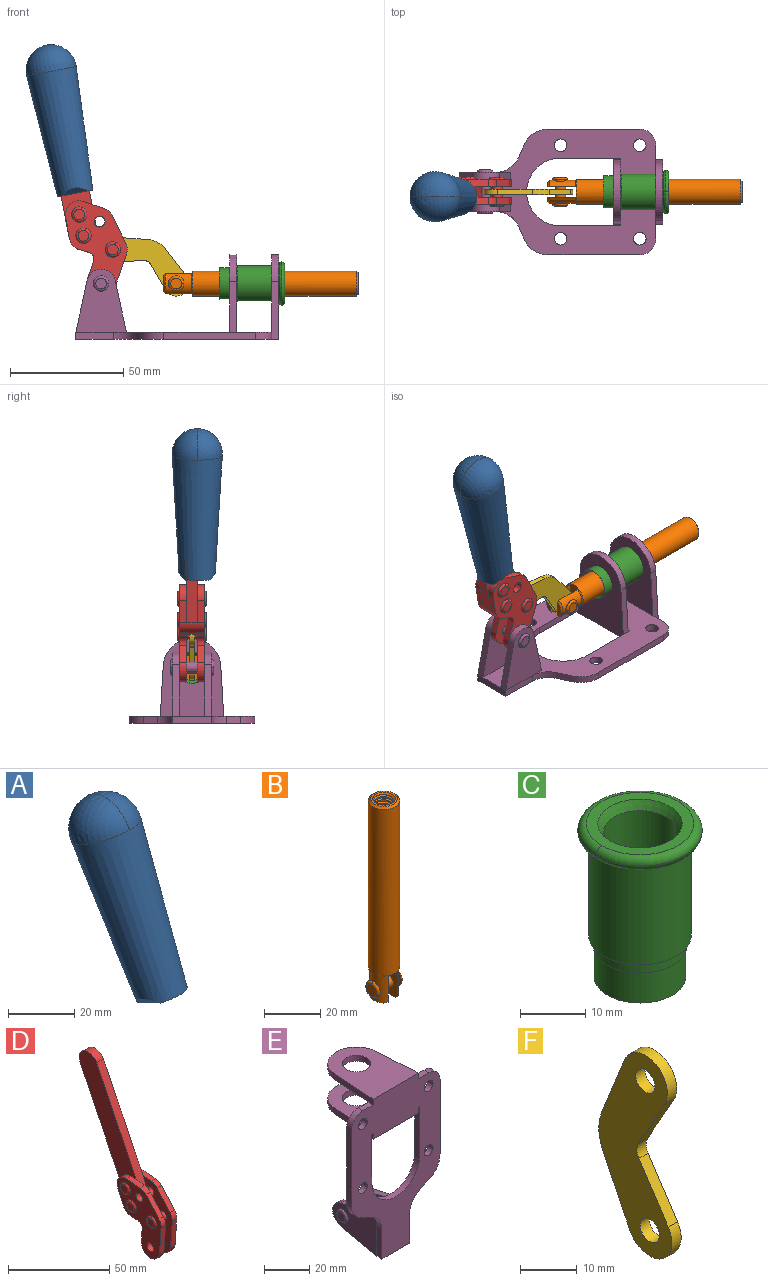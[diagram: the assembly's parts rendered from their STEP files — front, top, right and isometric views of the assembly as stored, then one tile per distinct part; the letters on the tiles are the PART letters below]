
ASSEMBLY  parts=6 mates=6
PART A: 11 faces, bbox 22.3x42.6x64.5 mm
  f0: sphere r=11.13mm, area 411.4mm2, adj f1,f8
  f1: cone r=11.11mm half-angle=3.3deg, axis (0,0.44,0.9), area 3251.8mm2, adj f0,f7,f8,f9,f10
  f2: cylinder r=6.16mm len=11.7mm, axis (1,0,0), area 89.5mm2, adj f3,f4,f5,f6
  f3: plane 60.23x36.75mm, normal (-1,0,0), area 763.6mm2, adj f2,f4,f6,f10
  f4: plane 51.37x25.05mm, normal (0,0.9,-0.44), area 264.2mm2, adj f2,f3,f5,f10
  f5: plane 60.23x36.75mm, normal (1,0,0), area 763.6mm2, adj f2,f4,f6,f10
  f6: plane 51.37x25.05mm, normal (0,-0.9,0.44), area 264.2mm2, adj f2,f3,f5,f10
  f7: plane 9.95x5.95mm, normal (0.71,-0.31,-0.64), area 25.8mm2, adj f1,f10
  f8: sphere r=11.13mm, area 411.4mm2, adj f0,f1
  f9: plane 9.95x5.95mm, normal (-0.71,-0.31,-0.64), area 25.8mm2, adj f1,f10
  f10: plane 14.27x11.38mm, normal (0,-0.44,-0.9), area 106.7mm2, adj f1,f3,f4,f5,f6,f7,f9
PART B: 48 faces, bbox 12.6x11.1x86.1 mm
  f0: torus R=2.41mm, axis (-1,0,0), area 15mm2, adj f30,f32,f34
  f1: torus R=2.41mm, axis (-1,0,0), area 15mm2, adj f29,f31,f33
  f2: cylinder r=5.54mm len=72.39mm, axis (0,0,1), area 2518.5mm2, adj f3,f4,f42,f43
  f3: cone r=5.54mm half-angle=45deg, axis (0,0,1), area 7.6mm2, adj f2,f5,f41
  f4: cone r=5.54mm half-angle=45deg, axis (0,0,-1), area 34.9mm2, adj f2,f39
  f5: cylinder r=5.08mm len=11.48mm, axis (0,0,1), area 108.3mm2, adj f3,f7,f8,f41
  f6: cylinder r=2.41mm len=4.83mm, axis (-1,0,0), area 71.2mm2, adj f40,f41
  f7: cylinder r=2.41mm len=4.83mm, axis (-1,0,0), area 7.6mm2, adj f5,f34
  f8: cone r=5.08mm half-angle=45deg, axis (0,0,1), area 10.6mm2, adj f5,f37,f41
  f9: cone r=3.98mm half-angle=45deg, axis (0,0,1), area 17.6mm2, adj f27,f39,f45,f46,f47
  f10: cylinder r=2.41mm len=4.83mm, axis (-1,0,0), area 7.6mm2, adj f33,f38
  f11: cylinder r=3.2mm len=6.4mm, axis (0,0,1), area 78.4mm2, adj f12,f28,f44,f45,f47
  f12: cylinder r=3.2mm len=6.4mm, axis (0,0,1), area 10.5mm2, adj f11,f13,f45,f47
  f13: cylinder r=3.2mm len=6.4mm, axis (0,0,1), area 10.5mm2, adj f12,f14,f45,f47
  f14: cylinder r=3.2mm len=6.4mm, axis (0,0,1), area 10.5mm2, adj f13,f15,f45,f47
  f15: cylinder r=3.2mm len=6.4mm, axis (0,0,1), area 10.5mm2, adj f14,f16,f45,f47
  f16: cylinder r=3.2mm len=6.4mm, axis (0,0,1), area 10.5mm2, adj f15,f17,f45,f47
  f17: cylinder r=3.2mm len=6.4mm, axis (0,0,1), area 10.5mm2, adj f16,f18,f45,f47
  f18: cylinder r=3.2mm len=6.4mm, axis (0,0,1), area 10.5mm2, adj f17,f19,f45,f47
  f19: cylinder r=3.2mm len=6.4mm, axis (0,0,1), area 10.5mm2, adj f18,f20,f45,f47
  f20: cylinder r=3.2mm len=6.4mm, axis (0,0,1), area 10.5mm2, adj f19,f21,f45,f47
  f21: cylinder r=3.2mm len=6.4mm, axis (0,0,1), area 10.5mm2, adj f20,f22,f45,f47
  f22: cylinder r=3.2mm len=6.4mm, axis (0,0,1), area 10.5mm2, adj f21,f23,f45,f47
  f23: cylinder r=3.2mm len=6.4mm, axis (0,0,1), area 10.5mm2, adj f22,f24,f45,f47
  f24: cylinder r=3.2mm len=6.4mm, axis (0,0,1), area 10.5mm2, adj f23,f25,f45,f47
  f25: cylinder r=3.2mm len=6.4mm, axis (0,0,1), area 10.5mm2, adj f24,f26,f45,f47
  f26: cylinder r=3.2mm len=6.4mm, axis (0,0,1), area 10.5mm2, adj f25,f27,f45,f47
  f27: cylinder r=3.2mm len=6.4mm, axis (0,0,1), area 7.4mm2, adj f9,f26,f45,f47
  f28: cone r=3.2mm half-angle=60deg, axis (0,0,1), area 37.2mm2, adj f11
  f29: plane 4.83x4.83mm, normal (-1,0,0), area 18.3mm2, adj f1,f31
  f30: plane 4.83x4.83mm, normal (1,0,0), area 18.3mm2, adj f0,f32
  f31: torus R=2.41mm, axis (-1,0,0), area 15mm2, adj f1,f29,f33
  f32: torus R=2.41mm, axis (-1,0,0), area 15mm2, adj f0,f30,f34
  f33: plane 6.83x6.83mm, normal (1,0,0), area 18.3mm2, adj f1,f10,f31
  f34: plane 6.83x6.83mm, normal (-1,0,0), area 18.3mm2, adj f0,f7,f32
  f35: cone r=5.08mm half-angle=45deg, axis (0,0,1), area 10.6mm2, adj f36,f38,f40
  f36: plane 7.25x1.97mm, normal (0,0,-1), area 10mm2, adj f35,f40
  f37: plane 7.25x1.97mm, normal (0,0,-1), area 10mm2, adj f8,f41
  f38: cylinder r=5.08mm len=11.48mm, axis (0,0,1), area 108.3mm2, adj f10,f35,f40,f42
  f39: plane 9.55x9.55mm, normal (0,0,1), area 22mm2, adj f4,f9
  f40: plane 12.76x10.09mm, normal (1,0,0), area 95.7mm2, adj f6,f35,f36,f38,f42,f43
  f41: plane 12.76x10.09mm, normal (-1,0,0), area 95.7mm2, adj f3,f5,f6,f8,f37,f43
  f42: cone r=5.54mm half-angle=45deg, axis (0,0,1), area 7.6mm2, adj f2,f38,f40
  f43: plane 11.07x4.7mm, normal (0,0,-1), area 50.4mm2, adj f2,f40,f41
  f44: plane 0.89x0.62mm, normal (-1,0,0), area 0.3mm2, adj f11,f45,f46,f47
  f45: bspline ~24.8x7.63mm, area 266.6mm2, adj f9,f11,f12,f13,f14,f15,f16,f17
  f46: bspline ~24.87x7.63mm, area 73.6mm2, adj f9,f44,f45,f47
  f47: bspline ~24.98x7.63mm, area 272.5mm2, adj f9,f11,f12,f13,f14,f15,f16,f17
PART C: 15 faces, bbox 20.6x20.6x28.7 mm
  f0: torus R=8.26mm, axis (0,0,1), area 56.8mm2, adj f1,f10,f12
  f1: torus R=8.26mm, axis (0,0,1), area 56.8mm2, adj f0,f6,f13
  f2: cylinder r=5.59mm len=25.91mm, axis (0,0,1), area 909.6mm2, adj f3,f4
  f3: cone r=6.86mm half-angle=45deg, axis (0,0,-1), area 70.2mm2, adj f2,f14
  f4: cone r=6.47mm half-angle=30deg, axis (0,0,1), area 66.7mm2, adj f2,f13
  f5: cylinder r=7.04mm len=14.07mm, axis (0,0,1), area 252.6mm2, adj f11,f14
  f6: torus R=8.26mm, axis (0,0,1), area 56.8mm2, adj f1,f12,f13
  f7: cylinder r=7.16mm len=14.33mm, axis (0,0,1), area 91.5mm2, adj f9,f11
  f8: cylinder r=7.86mm len=18.42mm, axis (0,0,1), area 909.6mm2, adj f9,f10
  f9: plane 15.72x15.72mm, normal (0,0,-1), area 33mm2, adj f7,f8
  f10: plane 16.51x16.51mm, normal (0,0,-1), area 19.9mm2, adj f0,f8,f12
  f11: plane 14.33x14.33mm, normal (0,0,-1), area 5.7mm2, adj f5,f7
  f12: torus R=8.26mm, axis (0,0,1), area 56.8mm2, adj f0,f6,f10
  f13: plane 16.51x16.51mm, normal (0,0,1), area 82.7mm2, adj f1,f4,f6
  f14: plane 14.07x14.07mm, normal (0,0,-1), area 7.8mm2, adj f3,f5
PART D: 59 faces, bbox 12.9x60.2x99.6 mm
  f0: torus R=2.39mm, axis (-1,0,0), area 14.9mm2, adj f20,f43,f51
  f1: torus R=2.39mm, axis (-1,0,0), area 14.9mm2, adj f19,f42,f51
  f2: torus R=2.39mm, axis (-1,0,0), area 14.9mm2, adj f18,f35,f51
  f3: torus R=2.39mm, axis (-1,0,0), area 14.9mm2, adj f14,f17,f23
  f4: torus R=2.39mm, axis (-1,0,0), area 14.9mm2, adj f13,f16,f23
  f5: torus R=2.39mm, axis (-1,0,0), area 14.9mm2, adj f12,f15,f23
  f6: cylinder r=2.39mm len=4.78mm, axis (1,0,0), area 46.5mm2, adj f48,f50,f51
  f7: cylinder r=2.39mm len=4.78mm, axis (1,0,0), area 46.5mm2, adj f50,f51
  f8: cylinder r=6.35mm len=12.68mm, axis (1,0,0), area 61.8mm2, adj f38,f39,f50,f51
  f9: cylinder r=2.39mm len=4.78mm, axis (-1,0,0), area 70.5mm2, adj f46,f50
  f10: cylinder r=2.39mm len=4.78mm, axis (-1,0,0), area 46.5mm2, adj f23,f45,f46
  f11: cylinder r=2.39mm len=4.78mm, axis (-1,0,0), area 46.5mm2, adj f23,f46
  f12: plane 4.78x4.78mm, normal (1,0,0), area 17.9mm2, adj f5,f15
  f13: plane 4.78x4.78mm, normal (1,0,0), area 17.9mm2, adj f4,f16
  f14: plane 4.78x4.78mm, normal (1,0,0), area 17.9mm2, adj f3,f17
  f15: torus R=2.39mm, axis (-1,0,0), area 14.9mm2, adj f5,f12,f23
  f16: torus R=2.39mm, axis (-1,0,0), area 14.9mm2, adj f4,f13,f23
  f17: torus R=2.39mm, axis (-1,0,0), area 14.9mm2, adj f3,f14,f23
  f18: plane 4.78x4.78mm, normal (-1,0,0), area 17.9mm2, adj f2,f35
  f19: plane 4.78x4.78mm, normal (-1,0,0), area 17.9mm2, adj f1,f42
  f20: plane 4.78x4.78mm, normal (-1,0,0), area 17.9mm2, adj f0,f43
  f21: plane 2.26x0.2mm, normal (1,0,0), area 0.2mm2, adj f31,f44
  f22: plane 2.26x0.2mm, normal (-1,0,0), area 0.2mm2, adj f41,f44
  f23: plane 39.37x30.77mm, normal (1,0,0), area 565.5mm2, adj f3,f4,f5,f10,f11,f15,f16,f17
  f24: cylinder r=6.1mm len=4.15mm, axis (-1,0,0), area 14.7mm2, adj f23,f25,f32,f46
  f25: plane 10.25x9.01mm, normal (0,-0.75,0.66), area 42.3mm2, adj f23,f24,f26,f46
  f26: cylinder r=6.35mm len=4.64mm, axis (-1,0,0), area 15.6mm2, adj f23,f25,f27,f46
  f27: plane 15.84x3.1mm, normal (0,-1,-0.07), area 49.2mm2, adj f23,f26,f28,f46
  f28: cylinder r=6.35mm len=12.68mm, axis (-1,0,0), area 61.8mm2, adj f23,f27,f29,f46
  f29: plane 8.11x3.1mm, normal (0,1,0.07), area 25.2mm2, adj f23,f28,f30,f46
  f30: cylinder r=3.05mm len=3.25mm, axis (-1,0,0), area 14.8mm2, adj f23,f29,f31,f46
  f31: plane 5.99x3.1mm, normal (0,0.07,-1), area 18.6mm2, adj f21,f23,f30,f44,f46
  f32: plane 9.5x3.1mm, normal (0,-0.07,1), area 29.5mm2, adj f23,f24,f33,f46,f47
  f33: cylinder r=6.1mm len=8.63mm, axis (-1,0,0), area 39.1mm2, adj f23,f32,f34,f47
  f34: plane 8.65x3.96mm, normal (0,0.91,-0.42), area 29.5mm2, adj f23,f33,f44,f47
  f35: torus R=2.39mm, axis (-1,0,0), area 14.9mm2, adj f2,f18,f51
  f36: plane 10.25x9.01mm, normal (0,-0.75,0.66), area 42.3mm2, adj f37,f49,f50,f51
  f37: cylinder r=6.35mm len=4.64mm, axis (1,0,0), area 15.6mm2, adj f36,f38,f50,f51
  f38: plane 15.84x3.1mm, normal (0,-1,-0.07), area 49.2mm2, adj f8,f37,f50,f51
  f39: plane 8.11x3.1mm, normal (0,1,0.07), area 25.2mm2, adj f8,f40,f50,f51
  f40: cylinder r=3.05mm len=3.25mm, axis (1,0,0), area 14.8mm2, adj f39,f41,f50,f51
  f41: plane 5.99x3.1mm, normal (0,0.07,-1), area 18.6mm2, adj f22,f40,f44,f50,f51
  f42: torus R=2.39mm, axis (-1,0,0), area 14.9mm2, adj f1,f19,f51
  f43: torus R=2.39mm, axis (-1,0,0), area 14.9mm2, adj f0,f20,f51
  f44: cylinder r=6.35mm len=12.12mm, axis (-1,0,0), area 128.9mm2, adj f21,f22,f23,f31,f34,f41,f46,f47
  f45: plane 2.65x1.35mm, normal (1,0,0), area 1mm2, adj f10,f55
  f46: plane 39.08x20.42mm, normal (-1,0,0), area 412.5mm2, adj f9,f10,f11,f24,f25,f26,f27,f28
  f47: plane 77.62x39.82mm, normal (1,0,0), area 850mm2, adj f32,f33,f34,f44,f53,f54,f55
  f48: plane 2.65x1.35mm, normal (-1,0,0), area 1mm2, adj f6,f55
  f49: cylinder r=6.1mm len=4.15mm, axis (1,0,0), area 14.7mm2, adj f36,f50,f51,f56
  f50: plane 39.08x20.42mm, normal (1,0,0), area 412.5mm2, adj f6,f7,f8,f9,f36,f37,f38,f39
  f51: plane 39.37x30.77mm, normal (-1,0,0), area 565.5mm2, adj f0,f1,f2,f6,f7,f8,f35,f36
  f52: plane 8.65x3.96mm, normal (0,0.91,-0.42), area 29.5mm2, adj f44,f51,f57,f58
  f53: plane 68.49x33.4mm, normal (0,0.9,-0.44), area 358.1mm2, adj f44,f47,f54,f58
  f54: cylinder r=6.35mm len=12.06mm, axis (1,0,0), area 93.7mm2, adj f47,f53,f55,f58
  f55: plane 68.49x33.4mm, normal (0,-0.9,0.44), area 358.1mm2, adj f44,f45,f46,f47,f48,f50,f54,f58
  f56: plane 9.5x3.1mm, normal (0,-0.07,1), area 29.5mm2, adj f49,f50,f51,f57,f58
  f57: cylinder r=6.1mm len=8.63mm, axis (1,0,0), area 39.1mm2, adj f51,f52,f56,f58
  f58: plane 77.62x39.82mm, normal (-1,0,0), area 850mm2, adj f44,f52,f53,f54,f55,f56,f57
PART E: 55 faces, bbox 55.7x37.4x89.8 mm
  f0: torus R=2.41mm, axis (-1,0,0), area 15mm2, adj f11,f15,f25
  f1: torus R=2.41mm, axis (-1,0,0), area 15mm2, adj f10,f12,f22
  f2: cylinder r=2.78mm len=5.56mm, axis (0,-1,0), area 54.2mm2, adj f30,f54
  f3: cylinder r=14.99mm len=29.97mm, axis (0,-1,0), area 145.9mm2, adj f30,f49,f53,f54
  f4: cylinder r=2.78mm len=5.56mm, axis (0,-1,0), area 54.2mm2, adj f30,f54
  f5: cylinder r=2.78mm len=5.56mm, axis (0,-1,0), area 54.2mm2, adj f30,f54
  f6: cylinder r=2.78mm len=5.56mm, axis (0,-1,0), area 54.2mm2, adj f30,f54
  f7: cylinder r=6.35mm len=12.7mm, axis (0,0,1), area 123.6mm2, adj f27,f51
  f8: cylinder r=6.35mm len=12.7mm, axis (0,0,-1), area 124.7mm2, adj f21,f35
  f9: cylinder r=2.41mm len=11.18mm, axis (-1,0,0), area 169.4mm2, adj f16,f19
  f10: plane 4.83x4.83mm, normal (1,0,0), area 18.3mm2, adj f1,f12
  f11: plane 4.83x4.83mm, normal (-1,0,0), area 18.3mm2, adj f0,f15
  f12: torus R=2.41mm, axis (-1,0,0), area 15mm2, adj f1,f10,f22
  f13: cylinder r=6.35mm len=12.41mm, axis (1,0,0), area 53.4mm2, adj f18,f19,f22,f23
  f14: cylinder r=6.35mm len=12.41mm, axis (-1,0,0), area 53.4mm2, adj f16,f17,f24,f25
  f15: torus R=2.41mm, axis (-1,0,0), area 15mm2, adj f0,f11,f25
  f16: plane 27.86x22.35mm, normal (1,0,0), area 425.4mm2, adj f9,f14,f17,f24,f30
  f17: plane 22.86x4.97mm, normal (0,0.21,0.98), area 72.5mm2, adj f14,f16,f25,f30
  f18: plane 22.86x4.97mm, normal (0,0.21,0.98), area 72.5mm2, adj f13,f19,f22,f30
  f19: plane 27.86x22.35mm, normal (-1,0,0), area 425.4mm2, adj f9,f13,f18,f23,f30
  f20: cylinder r=12.7mm len=25.35mm, axis (0,0,-1), area 119.8mm2, adj f21,f34,f35,f36
  f21: plane 34.21x28.07mm, normal (0,0,-1), area 702.4mm2, adj f8,f20,f30,f34,f36
  f22: plane 27.96x22.45mm, normal (1,0,0), area 407.2mm2, adj f1,f12,f13,f18,f23,f30,f42,f43
  f23: plane 22.86x4.97mm, normal (0,0.21,-0.98), area 72.5mm2, adj f13,f19,f22,f44
  f24: plane 22.86x4.97mm, normal (0,0.21,-0.98), area 72.5mm2, adj f14,f16,f25,f44
  f25: plane 27.86x22.35mm, normal (-1,0,0), area 407.1mm2, adj f0,f14,f15,f17,f24,f30,f45,f46
  f26: plane 3.1x0.95mm, normal (0,0,-1), area 2.7mm2, adj f30,f49,f50,f54
  f27: plane 34.21x28.07mm, normal (0,0,1), area 702.4mm2, adj f7,f28,f30,f50,f52
  f28: cylinder r=12.7mm len=25.35mm, axis (0,0,1), area 118.8mm2, adj f27,f50,f51,f52
  f29: plane 3.1x0.95mm, normal (0,0,-1), area 2.7mm2, adj f30,f52,f53,f54
  f30: plane 86.54x55.63mm, normal (0,1,0), area 2362.9mm2, adj f2,f3,f4,f5,f6,f16,f17,f18
  f31: plane 40.56x3.1mm, normal (-1,0,0), area 125.7mm2, adj f30,f32,f48,f54
  f32: cylinder r=7.11mm len=7.11mm, axis (0,-1,0), area 34.6mm2, adj f30,f31,f33,f54
  f33: plane 6.67x3.1mm, normal (0,0,1), area 20.4mm2, adj f30,f32,f34,f54
  f34: plane 25.39x3.13mm, normal (-1,0.06,0), area 79.5mm2, adj f20,f21,f33,f35,f54
  f35: plane 37.31x28.45mm, normal (0,0,1), area 789.9mm2, adj f8,f20,f34,f36,f54
  f36: plane 25.39x3.13mm, normal (1,0.06,0), area 79.5mm2, adj f20,f21,f35,f37,f54
  f37: plane 6.67x3.1mm, normal (0,0,1), area 20.4mm2, adj f30,f36,f38,f54
  f38: cylinder r=7.11mm len=7.11mm, axis (0,-1,0), area 34.6mm2, adj f30,f37,f39,f54
  f39: plane 40.56x3.1mm, normal (1,0,0), area 125.7mm2, adj f30,f38,f40,f54
  f40: cylinder r=11.18mm len=10.16mm, axis (0,-1,0), area 39.5mm2, adj f30,f39,f41,f54
  f41: plane 6.09x3.1mm, normal (0.42,0,-0.91), area 20.8mm2, adj f30,f40,f42,f54
  f42: cylinder r=11.18mm len=9.41mm, axis (0,-1,0), area 37.2mm2, adj f22,f30,f41,f43,f54
  f43: plane 16.5x3.1mm, normal (1,0,0), area 51.1mm2, adj f22,f42,f44,f54
  f44: plane 17.37x3.1mm, normal (0,0,-1), area 53.8mm2, adj f23,f24,f30,f43,f45,f54
  f45: plane 16.5x3.1mm, normal (-1,0,0), area 51.1mm2, adj f25,f44,f46,f54
  f46: cylinder r=11.18mm len=9.41mm, axis (0,-1,0), area 37.2mm2, adj f25,f30,f45,f47,f54
  f47: plane 6.09x3.1mm, normal (-0.42,0,-0.91), area 20.8mm2, adj f30,f46,f48,f54
  f48: cylinder r=11.18mm len=10.16mm, axis (0,-1,0), area 39.5mm2, adj f30,f31,f47,f54
  f49: plane 26.54x3.1mm, normal (-1,0,0), area 82.3mm2, adj f3,f26,f30,f54
  f50: plane 25.39x3.1mm, normal (1,0.06,0), area 78.8mm2, adj f26,f27,f28,f51,f54
  f51: plane 37.31x28.45mm, normal (0,0,-1), area 789.9mm2, adj f7,f28,f50,f52,f54
  f52: plane 25.39x3.1mm, normal (-1,0.06,0), area 78.8mm2, adj f27,f28,f29,f51,f54
  f53: plane 26.54x3.1mm, normal (1,0,0), area 82.3mm2, adj f3,f29,f30,f54
  f54: plane 89.66x55.63mm, normal (0,-1,0), area 2678.5mm2, adj f2,f3,f4,f5,f6,f26,f29,f31
PART F: 12 faces, bbox 2.3x18.2x42.8 mm
  f0: cylinder r=2.4mm len=4.8mm, axis (1,0,0), area 34.9mm2, adj f4,f11
  f1: cylinder r=10.41mm len=8.47mm, axis (1,0,0), area 20.2mm2, adj f4,f9,f10,f11
  f2: cylinder r=3.05mm len=3.16mm, axis (1,0,0), area 7.7mm2, adj f4,f6,f7,f11
  f3: cylinder r=2.4mm len=4.8mm, axis (1,0,0), area 34.9mm2, adj f4,f11
  f4: plane 42.81x18.23mm, normal (-1,0,0), area 414.1mm2, adj f0,f1,f2,f3,f5,f6,f7,f8
  f5: cylinder r=5.54mm len=10.67mm, axis (1,0,0), area 41.8mm2, adj f4,f6,f10,f11
  f6: plane 11.66x6.53mm, normal (0,-0.87,-0.49), area 30.9mm2, adj f2,f4,f5,f11
  f7: plane 11.17x7.33mm, normal (0,-0.84,0.55), area 30.9mm2, adj f2,f4,f8,f11
  f8: cylinder r=5.54mm len=10.51mm, axis (1,0,0), area 41.8mm2, adj f4,f7,f9,f11
  f9: plane 13.67x6.67mm, normal (0,0.9,-0.44), area 35.1mm2, adj f1,f4,f8,f11
  f10: plane 14.1x5.7mm, normal (0,0.93,0.37), area 35.1mm2, adj f1,f4,f5,f11
  f11: plane 42.81x18.23mm, normal (1,0,0), area 414.1mm2, adj f0,f1,f2,f3,f5,f6,f7,f8
PLACE A rot(axis=(0.13,0.13,0.98),91deg) t=(-0.01,-2.31,49.24)mm
PLACE B rot(axis=(-0.58,0.58,-0.58),120deg) t=(-14.42,0,49.23)mm
PLACE C rot(axis=(0.71,0,0.71),180deg) t=(0,24.61,24.61)mm
PLACE D rot(axis=(0.13,0.13,0.98),91deg) t=(-0.01,0,49.24)mm
PLACE E rot(axis=(0.58,0.58,0.58),120deg) t=(0,0,0)mm fixed
PLACE F rot(axis=(0.47,-0.47,-0.75),106.2deg) t=(-23.91,0,10.71)mm
MATE fastened A.f2 <-> D.f54  axis (0,-1,0) through (-54.46,0,120.54)mm
MATE revolute D.f7 <-> E.f0  axis (0,-1,0) through (-32.09,0,24.61)mm
MATE slider B.f2 <-> C.f2  axis (1,0,0) through (44.36,0,24.61)mm
MATE revolute F.f3 <-> B.f6  axis (0,-1,0) through (1.05,0,24.61)mm
MATE fastened C.f2 <-> E.f7  axis (-1,0,0) through (46.39,0,24.61)mm
MATE revolute F.f5 <-> D.f4  axis (0,-1,0) through (-26.92,0,39.62)mm
